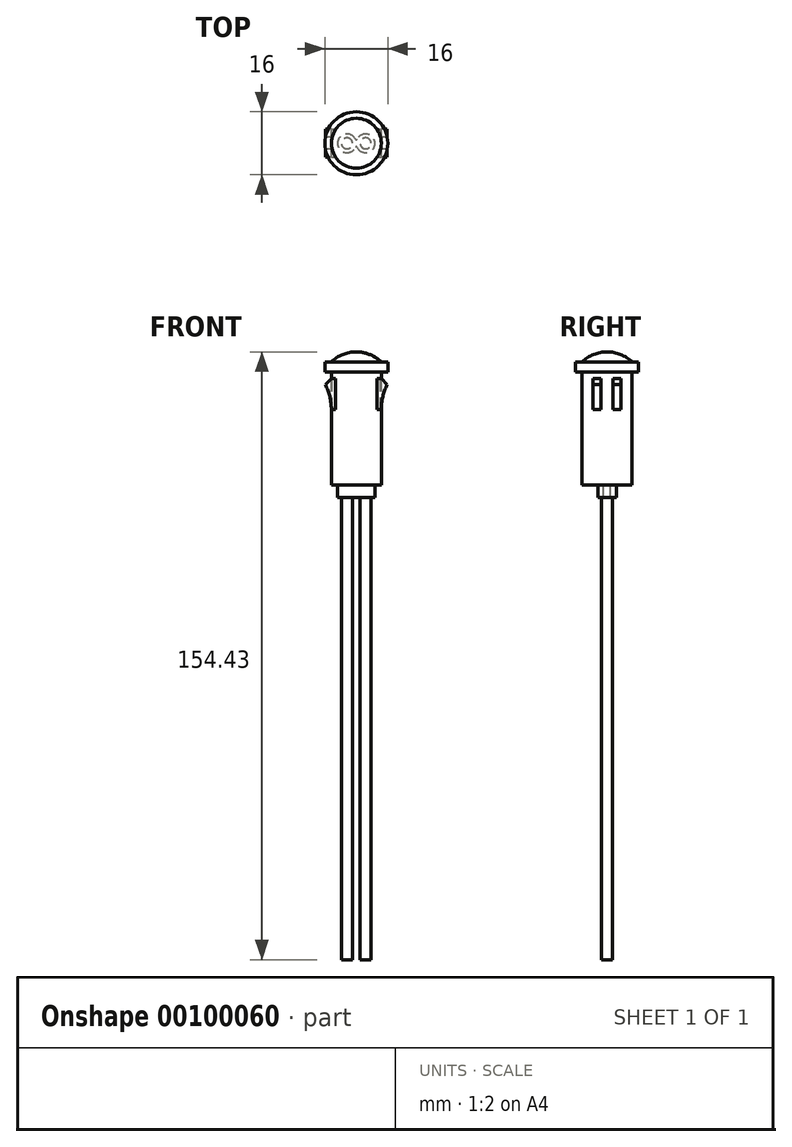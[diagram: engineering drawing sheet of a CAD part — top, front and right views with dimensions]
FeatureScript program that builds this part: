
annotation { "Feature Type Name" : "Feature", "Feature Type Description" : "" }
export const myFeature = defineFeature(function(context is Context, id is Id, definition is map)
    precondition{}
    {
        {
            var Q0;
            Q0=qCreatedBy(makeId("Top.planeOp"),FACE);
            var sketch = newSketch(context, id + "F0", { "sketchPlane" : qUnion([Q0])});
            skCircle(sketch, "E0", {"center": v(0, 0) * mm, "radius": 6.35 * mm});
            skSolve(sketch);
        }
        {
            var Q0;
            Q0 = qSketchRegion(id + "F0", true);
            extrude(context, id + "F1", {"entities" : qUnion([Q0]), "oppositeDirection" : true, "depth" : 28.7 * mm});
        }
        {
            var Q0;
            Q0=makeQuery(id+"F1.opExtrude","CAP_FACE",FACE,{"disambiguationData":[OSD([sQuery(id+"F0.wireOp",EDGE,"E0")])],"isStart":true});
            var sketch = newSketch(context, id + "F2", { "sketchPlane" : qUnion([Q0])});
            skCircle(sketch, "E1", {"center": v(0, 0) * mm, "radius": 8 * mm});
            skSolve(sketch);
        }
        {
            var Q0;
            Q0 = qSketchRegion(id + "F2", true);
            extrude(context, id + "F3", {"entities" : qUnion([Q0]), "operationType" : NewBodyOperationType.ADD, "depth" : 2.54 * mm});
        }
        {
            var Q0;
            Q0=qCreatedBy(makeId("Front.planeOp"),FACE);
            var sketch = newSketch(context, id + "F4", { "sketchPlane" : qUnion([Q0])});
            skArc(sketch, "E2", {"start": v(6.35, 2.54) * mm, "mid": v(3.42, 4.42) * mm, "end": v(0, 5.08) * mm});
            skLineSegment(sketch, "E3", {"start": v(0, 5.08) * mm, "end": v(0, 2.54) * mm});
            skLineSegment(sketch, "E4.0", {"start": v(0, 2.54) * mm, "end": v(6.35, 2.54) * mm});
            skSolve(sketch);
        }
        {
            var Q0;
            Q0=makeQuery(id+"F4.imprint","IMPRINT",FACE,{"disambiguationData":[TD([[makeQuery(id+"F4.imprint","IMPRINT",EDGE,{"derivedFrom":sQuery(id+"F4.wireOp",EDGE,"E2")}),1.0]])]});
            var Q1;
            Q1=sQuery(id+"F4.wireOp",EDGE,"E3");
            revolve(context, id + "F5", {"entities" : qUnion([Q0]), "axis" : qUnion([Q1]), "revolveType" : RevolveType.FULL});
        }
        {
            var Q0;
            Q0=makeQuery(id+"F1.opExtrude","CAP_FACE",FACE,{"disambiguationData":[OSD([sQuery(id+"F0.wireOp",EDGE,"E0")])],"isStart":false});
            var sketch = newSketch(context, id + "F6", { "sketchPlane" : qUnion([Q0])});
            skArc(sketch, "E5", {"start": v(0.23, -1.02) * mm, "mid": v(4.76, 0) * mm, "end": v(0.23, 1.02) * mm});
            skArc(sketch, "E6", {"start": v(-0.23, 1.02) * mm, "mid": v(-4.76, 0) * mm, "end": v(-0.23, -1.02) * mm});
            skLineSegment(sketch, "E7", {"start": v(-2.38, 0) * mm, "end": v(0, 0) * mm, "construction": true});
            skLineSegment(sketch, "E8", {"start": v(0, 0) * mm, "end": v(2.38, 0) * mm, "construction": true});
            skArc(sketch, "E9", {"start": v(-0.23, 1.02) * mm, "mid": v(0, 0.87) * mm, "end": v(0.23, 1.02) * mm});
            skArc(sketch, "E10", {"start": v(0.23, -1.02) * mm, "mid": v(0, -0.87) * mm, "end": v(-0.23, -1.02) * mm});
            skSolve(sketch);
        }
        {
            var Q0;
            Q0 = qSketchRegion(id + "F6", true);
            extrude(context, id + "F7", {"entities" : qUnion([Q0]), "operationType" : NewBodyOperationType.ADD, "depth" : 3.17 * mm});
        }
        {
            var Q0;
            Q0=makeQuery(id+"F7.opExtrude","CAP_FACE",FACE,{"disambiguationData":[OSD([sQuery(id+"F6.wireOp",EDGE,"E5"),sQuery(id+"F6.wireOp",EDGE,"E6"),sQuery(id+"F6.wireOp",EDGE,"E9"),sQuery(id+"F6.wireOp",EDGE,"E10")])],"isStart":false});
            var sketch = newSketch(context, id + "F8", { "sketchPlane" : qUnion([Q0])});
            skCircle(sketch, "E11", {"center": v(-2.38, 0) * mm, "radius": 1.4 * mm});
            skCircle(sketch, "E12", {"center": v(2.38, 0) * mm, "radius": 1.4 * mm});
            skSolve(sketch);
        }
        {
            var Q0;
            Q0 = qSketchRegion(id + "F8", true);
            extrude(context, id + "F9", {"entities" : qUnion([Q0]), "operationType" : NewBodyOperationType.ADD, "depth" : 117.47 * mm});
        }
        {
            var Q0;
            Q0=qCreatedBy(makeId("Front.planeOp"),FACE);
            var sketch = newSketch(context, id + "F10", { "sketchPlane" : qUnion([Q0])});
            skLineSegment(sketch, "E13", {"start": v(-6.35, -1.65) * mm, "end": v(6.35, -1.65) * mm});
            skLineSegment(sketch, "E14", {"start": v(-6.35, -1.65) * mm, "end": v(-7.85, -3.18) * mm});
            skLineSegment(sketch, "E15", {"start": v(-7.85, -3.18) * mm, "end": v(7.85, -3.18) * mm, "construction": true});
            skLineSegment(sketch, "E16", {"start": v(7.85, -3.18) * mm, "end": v(6.35, -1.65) * mm});
            skLineSegment(sketch, "E17", {"start": v(0, -3.18) * mm, "end": v(0, 0) * mm, "construction": true});
            skArc(sketch, "E18", {"start": v(-6.35, -9.53) * mm, "mid": v(-6.73, -6.26) * mm, "end": v(-7.85, -3.18) * mm});
            skArc(sketch, "E19", {"start": v(7.85, -3.17) * mm, "mid": v(6.73, -6.26) * mm, "end": v(6.35, -9.52) * mm});
            skLineSegment(sketch, "E20.0", {"start": v(-8, 0) * mm, "end": v(8, 0) * mm, "construction": true});
            skLineSegment(sketch, "E20.1", {"start": v(-6.35, -28.7) * mm, "end": v(6.35, -28.7) * mm, "construction": true});
            skLineSegment(sketch, "E21", {"start": v(-6.35, -28.7) * mm, "end": v(-6.35, 0) * mm, "construction": true});
            skLineSegment(sketch, "E22", {"start": v(6.35, -28.7) * mm, "end": v(6.35, 0) * mm, "construction": true});
            skLineSegment(sketch, "E23", {"start": v(-6.35, -9.53) * mm, "end": v(6.35, -9.53) * mm});
            skSolve(sketch);
        }
        {
            var Q0;
            Q0=makeQuery(id+"F10.imprint","IMPRINT",FACE,{"disambiguationData":[TD([[makeQuery(id+"F10.imprint","IMPRINT",EDGE,{"derivedFrom":sQuery(id+"F10.wireOp",EDGE,"E13")}),-1.0]])]});
            extrude(context, id + "F11", {"entities" : qUnion([Q0]), "operationType" : NewBodyOperationType.ADD, "depth" : 7.11 * mm, "symmetric" : true});
        }
        {
            var Q0;
            Q0=qCreatedBy(makeId("Right.planeOp"),FACE);
            var sketch = newSketch(context, id + "F12", { "sketchPlane" : qUnion([Q0])});
            skLineSegment(sketch, "E24.bottom", {"start": v(1.52, -1.4) * mm, "end": v(-1.52, -1.4) * mm});
            skLineSegment(sketch, "E24.top", {"start": v(1.52, -9.78) * mm, "end": v(-1.52, -9.78) * mm});
            skLineSegment(sketch, "E24.left", {"start": v(1.52, -1.4) * mm, "end": v(1.52, -9.78) * mm});
            skLineSegment(sketch, "E24.right", {"start": v(-1.52, -1.4) * mm, "end": v(-1.52, -9.78) * mm});
            skLineSegment(sketch, "E25.0", {"start": v(-3.56, -9.53) * mm, "end": v(-3.56, -3.18) * mm, "construction": true});
            skLineSegment(sketch, "E25.1", {"start": v(3.56, -9.53) * mm, "end": v(3.56, -3.18) * mm, "construction": true});
            skLineSegment(sketch, "E26", {"start": v(3.56, -6.35) * mm, "end": v(1.52, -6.35) * mm, "construction": true});
            skLineSegment(sketch, "E27", {"start": v(-1.52, -6.35) * mm, "end": v(-3.56, -6.35) * mm, "construction": true});
            skSolve(sketch);
        }
        {
            var Q0;
            Q0 = qSketchRegion(id + "F12", true);
            extrude(context, id + "F13", {"entities" : qUnion([Q0]), "operationType" : NewBodyOperationType.REMOVE, "oppositeDirection" : true, "depth" : 25.4 * mm, "symmetric" : true});
        }
        {
            var Q0;
            Q0=makeQuery(id+"F13.boolean.opBoolean","COPY",FACE,{"derivedFrom":makeQuery(id+"F13.opExtrude","SWEPT_FACE",FACE,{"disambiguationData":[OSD([sQuery(id+"F12.wireOp",EDGE,"E24.bottom")])]})});
            var sketch = newSketch(context, id + "F14", { "sketchPlane" : qUnion([Q0])});
            skArc(sketch, "E28.0", {"start": v(6.16, -1.52) * mm, "mid": v(6.35, 0) * mm, "end": v(6.16, 1.52) * mm});
            skArc(sketch, "E28.1", {"start": v(-6.16, 1.52) * mm, "mid": v(-6.35, 0) * mm, "end": v(-6.16, -1.52) * mm});
            skLineSegment(sketch, "E29.0", {"start": v(-6.16, 1.52) * mm, "end": v(6.16, 1.52) * mm});
            skLineSegment(sketch, "E29.1", {"start": v(-6.16, -1.52) * mm, "end": v(6.16, -1.52) * mm});
            skSolve(sketch);
        }
        {
            var Q0;
            Q0 = qSketchRegion(id + "F14", true);
            extrude(context, id + "F15", {"entities" : qUnion([Q0]), "operationType" : NewBodyOperationType.ADD, "depth" : 9.52 * mm});
        }
    });
